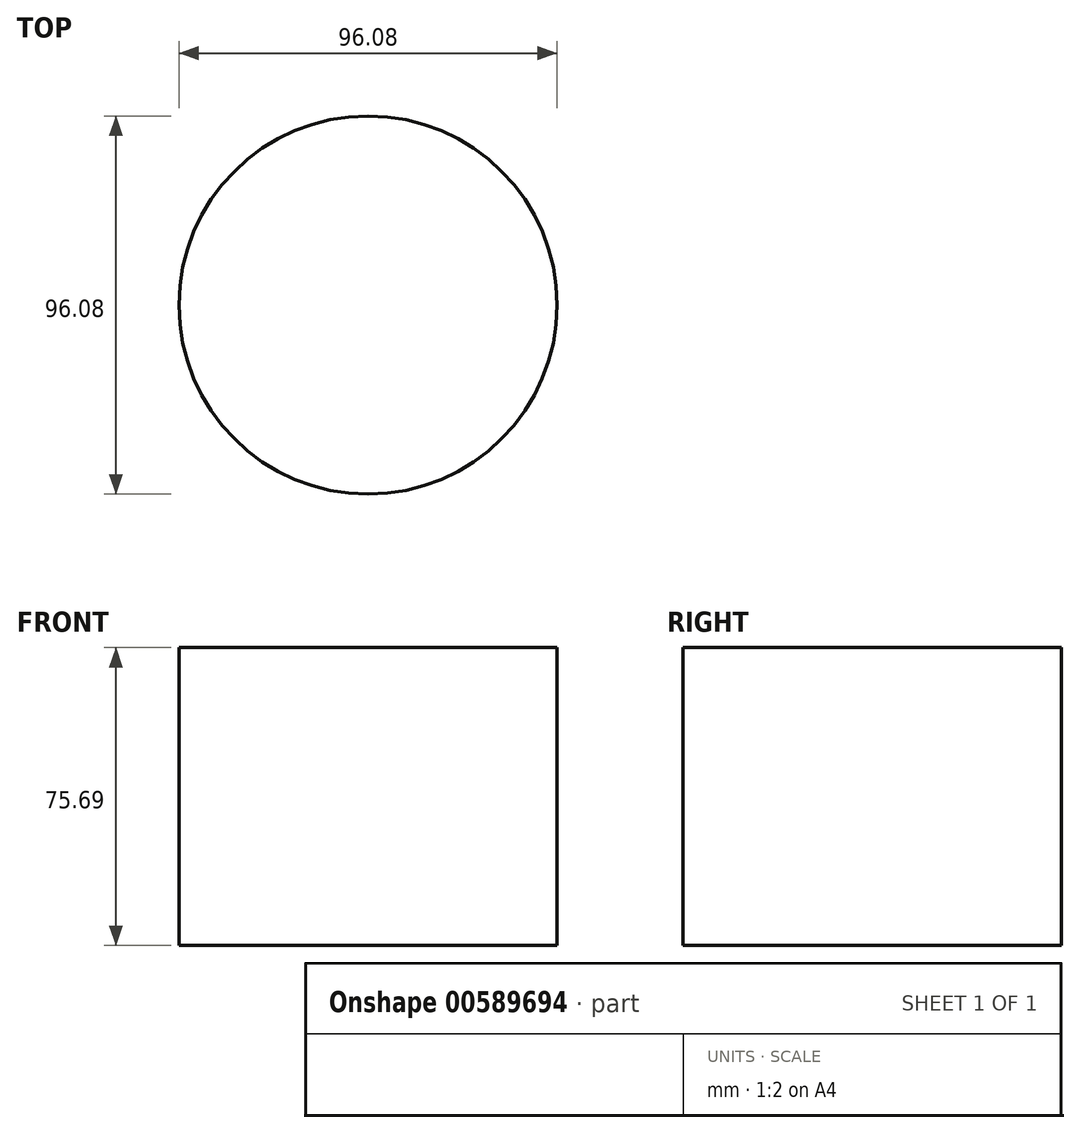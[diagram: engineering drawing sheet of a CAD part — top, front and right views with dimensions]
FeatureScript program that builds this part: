
annotation { "Feature Type Name" : "Feature", "Feature Type Description" : "" }
export const myFeature = defineFeature(function(context is Context, id is Id, definition is map)
    precondition{}
    {
        {
            var Q0;
            Q0=qCreatedBy(makeId("Top.planeOp"),FACE);
            var sketch = newSketch(context, id + "F0", { "sketchPlane" : qUnion([Q0])});
            skCircle(sketch, "E0", {"center": v(0, 0) * mm, "radius": 48.04 * mm});
            skSolve(sketch);
        }
        {
            var Q0;
            Q0=makeQuery(id+"F0.imprint","IMPRINT",FACE,{"disambiguationData":[TD([[makeQuery(id+"F0.imprint","IMPRINT",EDGE,{"derivedFrom":sQuery(id+"F0.wireOp",EDGE,"E0")}),1.0]])]});
            extrude(context, id + "F1", {"entities" : qUnion([Q0]), "depth" : 75.7 * mm, "offsetDistance" : 25.4 * mm});
        }
    });
